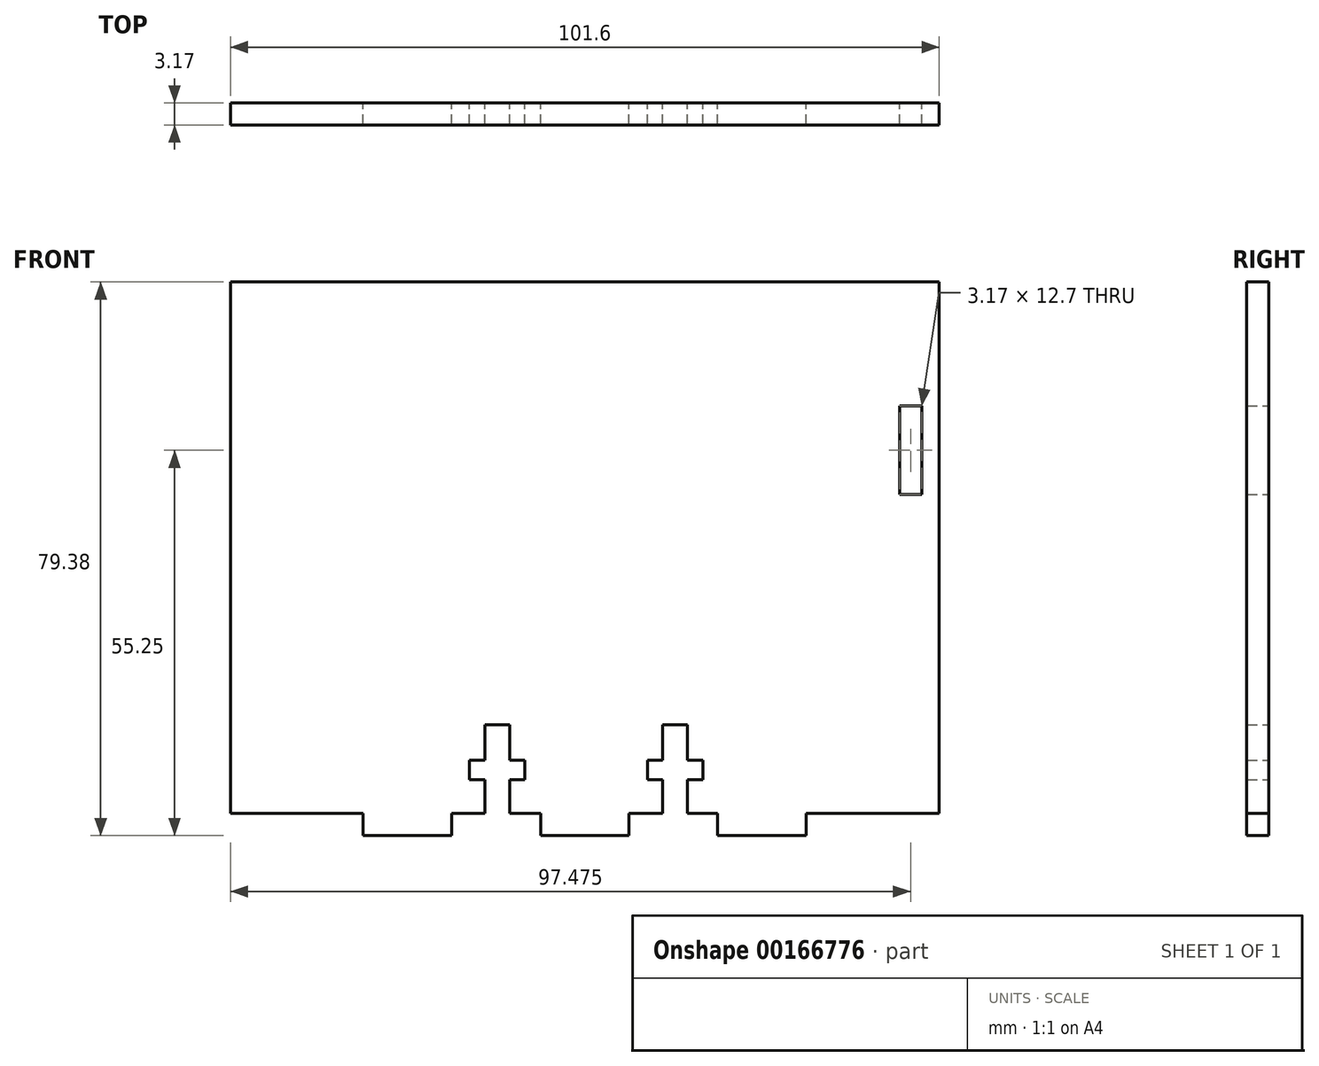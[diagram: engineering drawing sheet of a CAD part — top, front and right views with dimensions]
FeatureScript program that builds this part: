
annotation { "Feature Type Name" : "Feature", "Feature Type Description" : "" }
export const myFeature = defineFeature(function(context is Context, id is Id, definition is map)
    precondition{}
    {
        {
            var Q0;
            Q0=qCreatedBy(makeId("Front.planeOp"),FACE);
            var sketch = newSketch(context, id + "F0", { "sketchPlane" : qUnion([Q0])});
            skLineSegment(sketch, "E0.bottom", {"start": v(-50.98, 30.48) * mm, "end": v(50.62, 30.48) * mm});
            skLineSegment(sketch, "E0.top", {"start": v(-50.98, -45.72) * mm, "end": v(-14.53, -45.72) * mm});
            skLineSegment(sketch, "E0.left", {"start": v(-50.98, 30.48) * mm, "end": v(-50.98, -45.72) * mm});
            skLineSegment(sketch, "E0.right", {"start": v(50.62, 30.48) * mm, "end": v(50.62, -23.62) * mm});
            skLineSegment(sketch, "E1.trimOffspring", {"start": v(50.62, -27.18) * mm, "end": v(50.62, -45.72) * mm});
            skLineSegment(sketch, "E2", {"start": v(-14.53, -45.72) * mm, "end": v(-14.53, -40.88) * mm});
            skLineSegment(sketch, "E3", {"start": v(-14.53, -40.88) * mm, "end": v(-16.72, -40.88) * mm});
            skLineSegment(sketch, "E4", {"start": v(-16.72, -40.88) * mm, "end": v(-16.72, -38.1) * mm});
            skLineSegment(sketch, "E5", {"start": v(-16.72, -38.1) * mm, "end": v(-14.53, -38.1) * mm});
            skLineSegment(sketch, "E6", {"start": v(-14.53, -38.1) * mm, "end": v(-14.53, -33.02) * mm});
            skLineSegment(sketch, "E7", {"start": v(-14.53, -33.02) * mm, "end": v(-10.97, -33.02) * mm});
            skLineSegment(sketch, "E8", {"start": v(-10.97, -33.02) * mm, "end": v(-10.97, -38.1) * mm});
            skLineSegment(sketch, "E9", {"start": v(-10.97, -38.1) * mm, "end": v(-8.78, -38.1) * mm});
            skLineSegment(sketch, "E10", {"start": v(-8.78, -38.1) * mm, "end": v(-8.78, -40.88) * mm});
            skLineSegment(sketch, "E11", {"start": v(-8.78, -40.88) * mm, "end": v(-10.97, -40.88) * mm});
            skLineSegment(sketch, "E12", {"start": v(-10.97, -40.88) * mm, "end": v(-10.97, -45.72) * mm});
            skLineSegment(sketch, "E13.trimOffspring", {"start": v(-10.97, -45.72) * mm, "end": v(10.97, -45.72) * mm});
            skLineSegment(sketch, "E14.MirrorCS", {"start": v(10.97, -33.02) * mm, "end": v(10.97, -38.1) * mm});
            skLineSegment(sketch, "E15.MirrorCS", {"start": v(14.53, -45.72) * mm, "end": v(14.53, -40.88) * mm});
            skLineSegment(sketch, "E16.MirrorCS", {"start": v(10.97, -38.1) * mm, "end": v(8.78, -38.1) * mm});
            skLineSegment(sketch, "E17.MirrorCS", {"start": v(16.72, -40.88) * mm, "end": v(16.72, -38.1) * mm});
            skLineSegment(sketch, "E18.MirrorCS", {"start": v(14.53, -33.02) * mm, "end": v(10.97, -33.02) * mm});
            skLineSegment(sketch, "E19.MirrorCS", {"start": v(8.78, -40.88) * mm, "end": v(10.97, -40.88) * mm});
            skLineSegment(sketch, "E20.MirrorCS", {"start": v(10.97, -40.88) * mm, "end": v(10.97, -45.72) * mm});
            skLineSegment(sketch, "E21.MirrorCS", {"start": v(8.78, -38.1) * mm, "end": v(8.78, -40.88) * mm});
            skLineSegment(sketch, "E22.MirrorCS", {"start": v(14.53, -40.88) * mm, "end": v(16.72, -40.88) * mm});
            skLineSegment(sketch, "E23.MirrorCS", {"start": v(14.53, -38.1) * mm, "end": v(14.53, -33.02) * mm});
            skLineSegment(sketch, "E24.MirrorCS", {"start": v(16.72, -38.1) * mm, "end": v(14.53, -38.1) * mm});
            skLineSegment(sketch, "E25.trimOffspring", {"start": v(14.53, -45.72) * mm, "end": v(50.62, -45.72) * mm});
            skLineSegment(sketch, "E26", {"start": v(-31.93, -45.72) * mm, "end": v(-31.93, -48.9) * mm});
            skLineSegment(sketch, "E27", {"start": v(-31.93, -48.9) * mm, "end": v(-19.23, -48.9) * mm});
            skLineSegment(sketch, "E28", {"start": v(-19.23, -48.9) * mm, "end": v(-19.23, -45.72) * mm});
            skLineSegment(sketch, "E29", {"start": v(-6.53, -45.72) * mm, "end": v(-6.53, -48.9) * mm});
            skLineSegment(sketch, "E30", {"start": v(-6.53, -48.9) * mm, "end": v(6.17, -48.9) * mm});
            skLineSegment(sketch, "E31", {"start": v(6.17, -48.9) * mm, "end": v(6.17, -45.72) * mm});
            skLineSegment(sketch, "E32", {"start": v(31.57, -45.72) * mm, "end": v(31.57, -48.9) * mm});
            skLineSegment(sketch, "E33", {"start": v(31.57, -48.9) * mm, "end": v(18.87, -48.9) * mm});
            skLineSegment(sketch, "E34", {"start": v(18.87, -48.9) * mm, "end": v(18.87, -45.72) * mm});
            skPoint(sketch, "E35.end.orphan", {"position": v(53.8, 0) * mm});
            skLineSegment(sketch, "E36.bottom", {"start": v(44.9, 12.7) * mm, "end": v(48.08, 12.7) * mm});
            skLineSegment(sketch, "E36.top", {"start": v(44.9, 0) * mm, "end": v(48.08, 0) * mm});
            skLineSegment(sketch, "E36.left", {"start": v(44.9, 12.7) * mm, "end": v(44.9, 0) * mm});
            skLineSegment(sketch, "E36.right", {"start": v(48.08, 12.7) * mm, "end": v(48.08, 0) * mm});
            skLineSegment(sketch, "E37", {"start": v(50.62, -27.18) * mm, "end": v(50.62, -23.62) * mm});
            skSolve(sketch);
        }
        {
            var Q0;
            Q0 = qSketchRegion(id + "F0", true);
            extrude(context, id + "F1", {"entities" : qUnion([Q0]), "depth" : 3.17 * mm});
        }
    });
